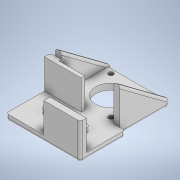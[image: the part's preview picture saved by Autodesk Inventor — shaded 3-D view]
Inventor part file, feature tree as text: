
AUTODESK INVENTOR PART (.ipt)
format: ipt  version: 2020 (Build 240168000, 168)  size: 285,184 bytes
history: native  units: in
note: dims shown in document units (in); Inventor stores cm internally (conversion verified against a paired STEP export)
features: extrude x12, sketch x12, chamfer x1, pattern_circular x1, fillet x1
ambient origin geometry x8: Origin, YZ Plane, XZ Plane, XY Plane, X Axis, Y Axis, Z Axis, Center Point
bodies: Solid1 (feature_tree)
feature tree (27):
  extrude  "Extrusion1"  Depth=1.4331in
  extrude  "Extrusion2"  Depth=1.1811in
  extrude  "Extrusion3"  Depth=1.1811in
  extrude  "Extrusion4"  Depth=0.9606in TaperAngle=0.0deg
  extrude  "Extrusion5"  Depth=0.3406in
  chamfer  "Chamfer1"  Distance=0.1969in
  extrude  "Extrusion6"  Depth=0.1575in
  extrude  "Extrusion7"  Depth=0.2362in
  extrude  "Extrusion8"  Depth=0.1181in TaperAngle=0.0deg
  extrude  "Extrusion9"  Depth=0.0787in
  extrude  "Extrusion10"  Depth=1.5866in
  extrude  "Extrusion11"  Depth=1.5866in
  extrude  "Extrusion12"  Depth=0.0787in TaperAngle=0.0deg
  pattern_circular  "Circular Pattern1"  [2 undecoded]
  fillet  "Fillet2"  Radius=0.1969in
  sketch  "Sketch1"  dims[d0=2.3937in d1=1.4331in]
  sketch  "Sketch2"  dims[d2=0.1969in d3=0.0in d4=1.1811in]
  sketch  "Sketch3"  dims[d5=0.1969in d6=1.1811in]
  sketch  "Sketch4"  dims[d7=0.1969in d8=0.9606in d9=0.0in]
  sketch  "Sketch5"  dims[d10=0.3406in d11=0.3406in d12=0.1969in d13=0.0in]
  sketch  "Sketch6"  dims[d14=0.1575in d15=0.1575in]
  sketch  "Sketch7"  dims[d16=0.5906in d17=0.0in d18=0.2362in]
  sketch  "Sketch8"  dims[d19=0.2362in d20=0.1181in d21=0.0in]
  sketch  "Sketch9"  dims[d22=0.0591in d23=0.0787in d24=45.0deg d26=2.5197in]
  sketch  "Sketch10"  dims[d27=1.5866in d28=0.0in d29=0.9843in]
  sketch  "Sketch11"  dims[d30=1.5866in d31=0.0in d32=0.2165in]
  sketch  "Sketch12"  dims[d33=0.2165in d34=1.378in d35=0.0in d36=0.1969in d37=0.1969in d38=1.1811in d39=0.0in d40=0.0787in d41=0.0in d42=2.1654in d43=0.0in d44=0.1181in d45=0.1575in d46=0.3937in d47=0.0in d48=1.5748in d49=360.0deg d51=0.0787in]
note: 2 required parameter values undecoded (feature->parameter linkage not recoverable at this tier; creation-order binding heuristic only, values carry confidence <= 0.55)
